# Revit family: 210_1418534f142b49fc87c5fddc121744
name_source: partatom
category: Mechanical Equipment
revit_build: Autodesk Revit 2018 (Build: 20170223_1515(x64)
units: mm (PartAtom-declared; Revit-internal decimal feet)

## family parameters
Always vertical = Yes
Cut with Voids When Loaded = No
Part Type = Breaks Into
Room Calculation Point = No
Round Connector Dimension = Use Diameter
Shared = No
Work Plane-Based = No

## types (6) — shared parameters
Description = DTV roof fan with vertical exhaust
H3 = 30 mm  [stored 0.0984252 ft]
Manufacturer = Exhausto
QmdConnectorList = 201;D
W = 500 mm
magiPartTypeId = 210
magiProductFamilyId = 1418534f142b49fc87c5fddc121744

## per-type parameters (varying)
| type | BL | D | H1 | H2 | ML | TY1 | X1 | magiProductId |
| DTV160-4-1 | 240 mm  [stored 0.787402 ft] | 160 mm | 70 mm  [stored 0.229659 ft] | 250 mm  [stored 0.82021 ft] | 310 mm  [stored 1.01706 ft] | No | 170 mm | 8da25bc93e8f4c8f8c5efd1122fbf3 |
| DTV450-4-1EC | 525 mm  [stored 1.72244 ft] | 450 mm | 220 mm  [stored 0.721785 ft] | 580 mm  [stored 1.90289 ft] | 650 mm  [stored 2.13255 ft] | Yes | 371 mm | ea518c36b7d341bca82dd82c3ebbdd |
| DTV400-4-1C | 525 mm  [stored 1.72244 ft] | 400 mm | 130 mm  [stored 0.426509 ft] | 490 mm  [stored 1.60761 ft] | 650 mm  [stored 2.13255 ft] | Yes | 371 mm | f29298aaa43840fbbe3e824b38b39e |
| DTV315-4-1EC | 465 mm  [stored 1.52559 ft] | 315 mm | 115 mm  [stored 0.377297 ft] | 405 mm  [stored 1.32874 ft] | 580 mm  [stored 1.90289 ft] | Yes | 329 mm | db386e11cde9493f891e08ba9584c3 |
| DTV250-4-1EC | 385 mm  [stored 1.26312 ft] | 250 mm | 100 mm  [stored 0.328084 ft] | 355 mm  [stored 1.1647 ft] | 485 mm  [stored 1.59121 ft] | Yes | 272 mm | 53c07ab0cae0422b920245742e0145 |
| DTV200-4-1 | 310 mm  [stored 1.01706 ft] | 200 mm | 80 mm  [stored 0.262467 ft] | 280 mm  [stored 0.918635 ft] | 390 mm  [stored 1.27953 ft] | No | 219 mm | 95ab10aa6cb046ac92bb948f281865 |

note: column(s) folded — value = type name in every type: MC Product Code

note: [stored X ft] marks values corroborated as IEEE doubles in the binary element streams (Revit-internal decimal feet)

## geometry (parser evidence)
native form markers: Sweep x1
no freeform markers — native parametric forms only
